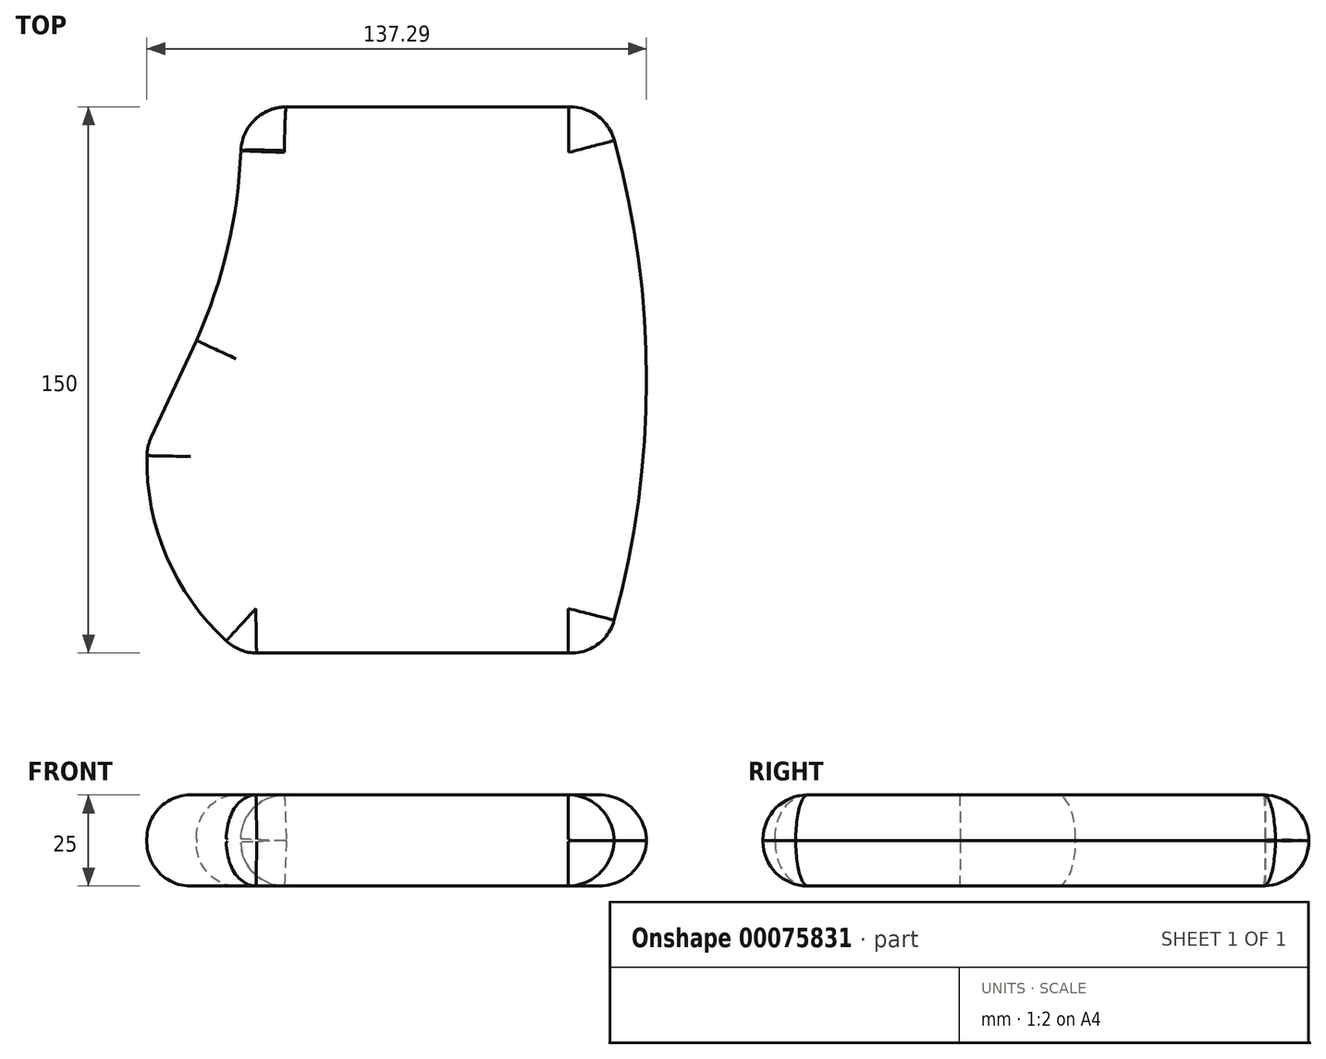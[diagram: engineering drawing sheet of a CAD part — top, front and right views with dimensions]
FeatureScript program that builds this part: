
annotation { "Feature Type Name" : "Feature", "Feature Type Description" : "" }
export const myFeature = defineFeature(function(context is Context, id is Id, definition is map)
    precondition{}
    {
        {
            var Q0;
            Q0=qCreatedBy(makeId("Top.planeOp"),FACE);
            var sketch = newSketch(context, id + "F0", { "sketchPlane" : qUnion([Q0])});
            skLineSegment(sketch, "E0.bottom", {"start": v(50, -75) * mm, "end": v(-50, -75) * mm});
            skPoint(sketch, "E0.middle", {"position": v(0, 0) * mm});
            skLineSegment(sketch, "E1", {"start": v(-50, 75) * mm, "end": v(50, 75) * mm});
            skArc(sketch, "E2", {"start": v(-62.17, 10.87) * mm, "mid": v(-52.3, 42.21) * mm, "end": v(-50, 75) * mm});
            skLineSegment(sketch, "E3", {"start": v(-62.17, 10.87) * mm, "end": v(-75.65, -18.16) * mm});
            skArc(sketch, "E4", {"start": v(-75.65, -18.16) * mm, "mid": v(-69.84, -49.75) * mm, "end": v(-50, -75) * mm});
            skArc(sketch, "E5", {"start": v(50, -75) * mm, "mid": v(61.52, 0) * mm, "end": v(50, 75) * mm});
            skSolve(sketch);
        }
        {
            var Q0;
            Q0 = qSketchRegion(id + "F0", true);
            extrude(context, id + "F1", {"entities" : qUnion([Q0]), "depth" : 25 * mm});
        }
        {
            var Q0;
            Q0=makeQuery(id+"F1.opExtrude","CAP_EDGE",EDGE,{"disambiguationData":[OSD([sQuery(id+"F0.wireOp",EDGE,"E5")])],"isStart":true});
            var Q1;
            Q1=makeQuery(id+"F1.opExtrude","CAP_EDGE",EDGE,{"disambiguationData":[OSD([sQuery(id+"F0.wireOp",EDGE,"E5")])],"isStart":false});
            fillet(context, id + "F2", {"entities" : qUnion([Q0, Q1]), "radius" : 13 * mm, "tangentPropagation" : true, "allowEdgeOverflow" : false});
        }
        {
            var Q0;
            Q0=makeQuery(id+"F1.opExtrude","CAP_EDGE",EDGE,{"disambiguationData":[OSD([sQuery(id+"F0.wireOp",EDGE,"E2")])],"isStart":true});
            var Q1;
            Q1=makeQuery(id+"F1.opExtrude","CAP_EDGE",EDGE,{"disambiguationData":[OSD([sQuery(id+"F0.wireOp",EDGE,"E2")])],"isStart":false});
            fillet(context, id + "F3", {"entities" : qUnion([Q0, Q1]), "radius" : 11 * mm, "tangentPropagation" : true, "allowEdgeOverflow" : false});
        }
        {
            var Q0;
            Q0=makeQuery(id+"F1.opExtrude","CAP_EDGE",EDGE,{"disambiguationData":[OSD([sQuery(id+"F0.wireOp",EDGE,"E0.bottom")])],"isStart":false});
            var Q1;
            Q1=makeQuery(id+"F1.opExtrude","CAP_EDGE",EDGE,{"disambiguationData":[OSD([sQuery(id+"F0.wireOp",EDGE,"E0.bottom")])],"isStart":true});
            fillet(context, id + "F4", {"entities" : qUnion([Q0, Q1]), "radius" : 12.2 * mm, "tangentPropagation" : true, "allowEdgeOverflow" : false});
        }
        {
            var Q0;
            Q0=makeQuery(id+"F1.opExtrude","CAP_EDGE",EDGE,{"disambiguationData":[OSD([sQuery(id+"F0.wireOp",EDGE,"E4")])],"isStart":true});
            fillet(context, id + "F5", {"entities" : qUnion([Q0]), "radius" : 12 * mm, "tangentPropagation" : true, "allowEdgeOverflow" : false});
        }
        {
            var Q0;
            Q0=makeQuery(id+"F5.opFillet","BLEND_EDGE",EDGE,{"blendedFrom":[makeQuery(id+"F1.opExtrude","CAP_EDGE",EDGE,{"disambiguationData":[OSD([sQuery(id+"F0.wireOp",EDGE,"E4")])],"isStart":true}),makeQuery(id+"F1.opExtrude","SWEPT_FACE",FACE,{"disambiguationData":[OSD([sQuery(id+"F0.wireOp",EDGE,"E3")])]})],"blendedInto":[makeQuery(id+"F1.opExtrude","SWEPT_FACE",FACE,{"disambiguationData":[OSD([sQuery(id+"F0.wireOp",EDGE,"E3")])]})]});
            fillet(context, id + "F6", {"entities" : qUnion([Q0]), "radius" : 12 * mm, "tangentPropagation" : true, "allowEdgeOverflow" : false});
        }
        {
            var Q0;
            Q0=makeQuery(id+"F1.opExtrude","CAP_EDGE",EDGE,{"disambiguationData":[OSD([sQuery(id+"F0.wireOp",EDGE,"E1")])],"isStart":false});
            fillet(context, id + "F7", {"entities" : qUnion([Q0]), "radius" : 12.5 * mm, "tangentPropagation" : true, "allowEdgeOverflow" : false});
        }
    });
